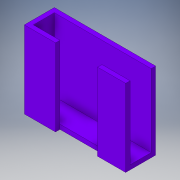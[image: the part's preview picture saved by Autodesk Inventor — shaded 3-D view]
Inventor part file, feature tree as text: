
AUTODESK INVENTOR PART (.ipt)
format: ipt  version: 2019 (Build 230136000, 136)  size: 130,560 bytes
history: native  units: mm
features: extrude x2, sketch x2, projected_geometry x1
ambient origin geometry x8: Origin, YZ Plane, XZ Plane, XY Plane, X Axis, Y Axis, Z Axis, Center Point
bodies: Solid1 (feature_tree)
feature tree (5):
  extrude  "Extrusion1"  Depth=15.0mm
  extrude  "Extrusion2"  Depth=72.18mm
  sketch  "Sketch1"  dims[d0=69.0mm d1=15.0mm]
  sketch  "Sketch2"  dims[d2=3.18mm d3=0.0mm d4=72.18mm d5=3.18mm d6=20.0mm d7=3.18mm d9=22.18mm d10=55.0mm d11=0.0mm]
  projected_geometry  "Projected Loop1"
